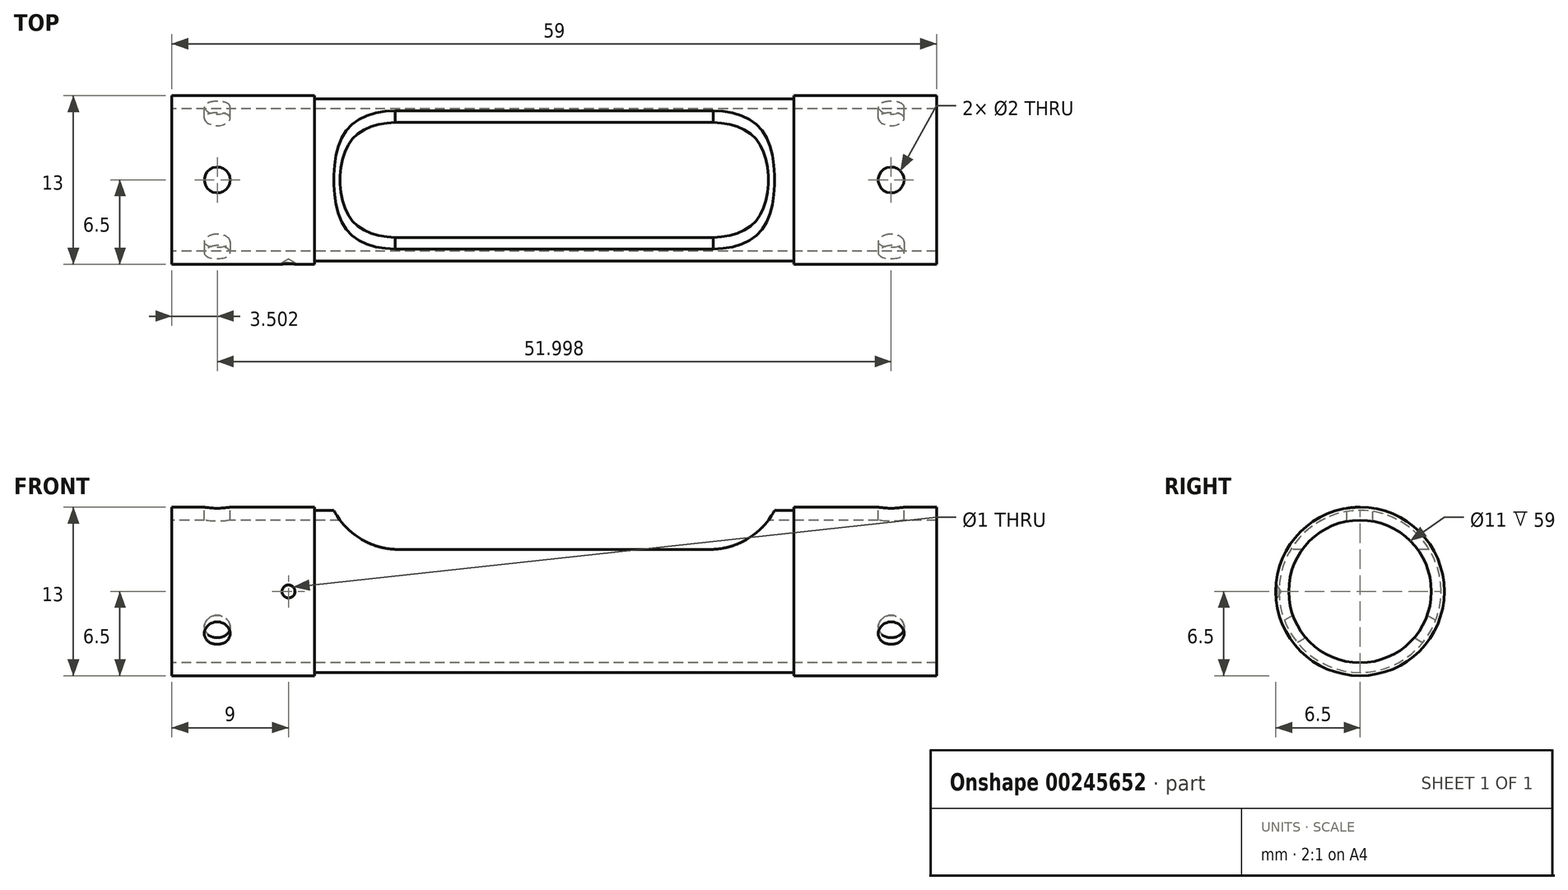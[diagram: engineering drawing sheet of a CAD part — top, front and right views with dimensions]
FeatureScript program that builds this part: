
annotation { "Feature Type Name" : "Feature", "Feature Type Description" : "" }
export const myFeature = defineFeature(function(context is Context, id is Id, definition is map)
    precondition{}
    {
        {
            var Q0;
            Q0=qCreatedBy(makeId("Right.planeOp"),FACE);
            var sketch = newSketch(context, id + "F0", { "sketchPlane" : qUnion([Q0])});
            skCircle(sketch, "E0", {"center": v(0, 0) * mm, "radius": 6.5 * mm});
            skCircle(sketch, "E1", {"center": v(0, 0) * mm, "radius": 5.5 * mm});
            skSolve(sketch);
        }
        {
            var Q0;
            Q0=makeQuery(id+"F0.imprint","IMPRINT",FACE,{"disambiguationData":[TD([[makeQuery(id+"F0.imprint","IMPRINT",EDGE,{"derivedFrom":sQuery(id+"F0.wireOp",EDGE,"E0")}),1.0]])]});
            extrude(context, id + "F1", {"entities" : qUnion([Q0]), "depth" : 11 * mm, "offsetDistance" : 25 * mm});
        }
        {
            var Q0;
            Q0=makeQuery(id+"F1.opExtrude","CAP_FACE",FACE,{"disambiguationData":[OSD([sQuery(id+"F0.wireOp",EDGE,"E0"),sQuery(id+"F0.wireOp",EDGE,"E1")])],"isStart":false});
            var sketch = newSketch(context, id + "F2", { "sketchPlane" : qUnion([Q0])});
            skCircle(sketch, "E2", {"center": v(0, 0) * mm, "radius": 6.25 * mm});
            skCircle(sketch, "E3", {"center": v(0, 0) * mm, "radius": 5.5 * mm});
            skSolve(sketch);
        }
        {
            var Q0;
            Q0=makeQuery(id+"F2.imprint","IMPRINT",FACE,{"disambiguationData":[TD([[makeQuery(id+"F2.imprint","IMPRINT",EDGE,{"derivedFrom":sQuery(id+"F2.wireOp",EDGE,"E2")}),1.0]])]});
            extrude(context, id + "F3", {"entities" : qUnion([Q0]), "operationType" : NewBodyOperationType.ADD, "depth" : 37 * mm, "offsetDistance" : 25 * mm});
        }
        {
            var Q0;
            Q0=makeQuery(id+"F3.opExtrude","CAP_FACE",FACE,{"disambiguationData":[OSD([sQuery(id+"F2.wireOp",EDGE,"E2"),sQuery(id+"F2.wireOp",EDGE,"E3")])],"isStart":false});
            var sketch = newSketch(context, id + "F4", { "sketchPlane" : qUnion([Q0])});
            skCircle(sketch, "E4", {"center": v(0, 0) * mm, "radius": 5.5 * mm});
            skCircle(sketch, "E5", {"center": v(0, 0) * mm, "radius": 6.5 * mm});
            skSolve(sketch);
        }
        {
            var Q0;
            Q0=makeQuery(id+"F4.imprint","IMPRINT",FACE,{"disambiguationData":[TD([[makeQuery(id+"F4.imprint","IMPRINT",EDGE,{"derivedFrom":sQuery(id+"F4.wireOp",EDGE,"E4")}),-1.0]])]});
            var Q1;
            Q1=makeQuery(id+"F4.imprint","IMPRINT",FACE,{"disambiguationData":[TD([[makeQuery(id+"F4.imprint","IMPRINT",EDGE,{"derivedFrom":sQuery(id+"F4.wireOp",EDGE,"E5")}),1.0]])]});
            extrude(context, id + "F5", {"entities" : qUnion([Q0, Q1]), "operationType" : NewBodyOperationType.ADD, "depth" : 11 * mm, "offsetDistance" : 25 * mm});
        }
        {
            var Q0;
            Q0=qCreatedBy(makeId("Front.planeOp"),FACE);
            cPlane(context, id + "F6", {"entities" : qUnion([Q0]), "cplaneType" : CPlaneType.OFFSET, "offset" : 6.5 * mm, "width" : 150 * mm, "height" : 150 * mm});
        }
        {
            var Q0;
            Q0=qCreatedBy(id+"F6.planeOp",FACE);
            var sketch = newSketch(context, id + "F7", { "sketchPlane" : qUnion([Q0])});
            skPoint(sketch, "E6", {"position": v(12.5, 6.25) * mm});
            skLineSegment(sketch, "E7", {"start": v(18.34, -6.25) * mm, "end": v(38.03, -6.25) * mm, "construction": true});
            skPoint(sketch, "E8.visualSharp", {"position": v(12.5, 3.25) * mm});
            skPoint(sketch, "E9", {"position": v(17.69, 3.25) * mm});
            skArc(sketch, "E10", {"start": v(12.5, 6.25) * mm, "mid": v(14.47, 4.11) * mm, "end": v(17.24, 3.25) * mm});
            skPoint(sketch, "E10.third.point", {"position": v(23.06, 9.25) * mm});
            skPoint(sketch, "E11.start.orphan", {"position": v(46.5, 9.25) * mm});
            skPoint(sketch, "E12.orphan", {"position": v(46.5, 3.25) * mm});
            skArc(sketch, "E13.MirrorCS", {"start": v(46.5, 6.25) * mm, "mid": v(44.53, 4.11) * mm, "end": v(41.76, 3.25) * mm});
            skLineSegment(sketch, "E14", {"start": v(17.24, 3.25) * mm, "end": v(41.76, 3.25) * mm});
            skLineSegment(sketch, "E15", {"start": v(12.5, 6.25) * mm, "end": v(46.5, 6.25) * mm});
            skSolve(sketch);
        }
        {
            var Q0;
            Q0 = qSketchRegion(id + "F7", true);
            extrude(context, id + "F8", {"entities" : qUnion([Q0]), "operationType" : NewBodyOperationType.REMOVE, "oppositeDirection" : true, "depth" : 25 * mm, "offsetDistance" : 25 * mm});
        }
        {
            var Q0;
            Q0=qCreatedBy(id+"F6.planeOp",FACE);
            var sketch = newSketch(context, id + "F9", { "sketchPlane" : qUnion([Q0])});
            skPoint(sketch, "E16", {"position": v(9, 0) * mm});
            skSolve(sketch);
        }
        {
            var Q0;
            Q0=sQuery(id+"F9.wireOp",VERTEX,"E16");
            var Q1;
            Q1=makeQuery(id+"F1.opExtrude","SWEPT_BODY",BODY,{"disambiguationData":[OSD([sQuery(id+"F0.wireOp",EDGE,"E0"),sQuery(id+"F0.wireOp",EDGE,"E1")])]});
            hole(context, id + "F10", {"style" : HoleStyle.SIMPLE, "endStyle" : HoleEndStyle.BLIND, "holeDiameter" : 1 * mm, "majorDiameter" : 5 * mm, "holeDepth" : .1 * mm, "isTappedThrough" : true, "tappedDepth" : 15 * mm, "tapClearance" : 0, "locations" : qUnion([Q0]), "scope" : qUnion([Q1]), "startStyle" : HoleStartStyle.SKETCH});
        }
        {
            var Q0;
            Q0=makeQuery(id+"F1.opExtrude","CAP_FACE",FACE,{"disambiguationData":[OSD([sQuery(id+"F0.wireOp",EDGE,"E0"),sQuery(id+"F0.wireOp",EDGE,"E1")])],"isStart":true});
            cPlane(context, id + "F11", {"entities" : qUnion([Q0]), "cplaneType" : CPlaneType.OFFSET, "offset" : 3.5 * mm, "oppositeDirection" : true, "width" : 150 * mm, "height" : 150 * mm});
        }
        {
            var Q0;
            Q0=qCreatedBy(id+"F11.planeOp",FACE);
            var sketch = newSketch(context, id + "F12", { "sketchPlane" : qUnion([Q0])});
            skLineSegment(sketch, "E17", {"start": v(0, 0) * mm, "end": v(0, 6.5) * mm});
            skLineSegment(sketch, "E18.1.0", {"start": v(0, 0) * mm, "end": v(-5.63, -3.25) * mm});
            skLineSegment(sketch, "E18.2.0", {"start": v(0, 0) * mm, "end": v(5.63, -3.25) * mm});
            skPoint(sketch, "E18.center", {"position": v(0, 0) * mm});
            skSolve(sketch);
        }
        {
            var Q0;
            Q0=sQuery(id+"F12.wireOp",VERTEX,"E17.end");
            var Q1;
            Q1=sQuery(id+"F12.wireOp",EDGE,"E17");
            cPlane(context, id + "F13", {"entities" : qUnion([Q0, Q1]), "cplaneType" : CPlaneType.CURVE_POINT, "offset" : 25 * mm, "width" : 150 * mm, "height" : 150 * mm});
        }
        {
            var Q0;
            Q0=qCreatedBy(id+"F13.planeOp",FACE);
            var sketch = newSketch(context, id + "F14", { "sketchPlane" : qUnion([Q0])});
            skPoint(sketch, "E19", {"position": v(3.5, 0) * mm});
            skPoint(sketch, "E20", {"position": v(0, 0) * mm});
            skCircle(sketch, "E21", {"center": v(3.5, 0) * mm, "radius": 1 * mm});
            skSolve(sketch);
        }
        {
            var Q0;
            Q0=makeQuery(id+"F14.imprint","IMPRINT",FACE,{"disambiguationData":[TD([[makeQuery(id+"F14.imprint","IMPRINT",EDGE,{"derivedFrom":sQuery(id+"F14.wireOp",EDGE,"E21")}),1.0]])]});
            extrude(context, id + "F15", {"entities" : qUnion([Q0]), "operationType" : NewBodyOperationType.REMOVE, "oppositeDirection" : true, "depth" : 5 * mm, "offsetDistance" : 25 * mm});
        }
        {
            var Q0;
            Q0=sQuery(id+"F12.wireOp",VERTEX,"E18.1.0.end");
            var Q1;
            Q1=sQuery(id+"F12.wireOp",EDGE,"E18.1.0");
            cPlane(context, id + "F16", {"entities" : qUnion([Q0, Q1]), "cplaneType" : CPlaneType.CURVE_POINT, "offset" : 25 * mm, "width" : 150 * mm, "height" : 150 * mm});
        }
        {
            var Q0;
            Q0=qCreatedBy(id+"F16.planeOp",FACE);
            var sketch = newSketch(context, id + "F17", { "sketchPlane" : qUnion([Q0])});
            skCircle(sketch, "E22", {"center": v(-3.5, 0) * mm, "radius": 1 * mm});
            skSolve(sketch);
        }
        {
            var Q0;
            Q0 = qSketchRegion(id + "F17", true);
            extrude(context, id + "F18", {"entities" : qUnion([Q0]), "operationType" : NewBodyOperationType.REMOVE, "oppositeDirection" : true, "depth" : 5 * mm, "offsetDistance" : 25 * mm});
        }
        {
            var Q0;
            Q0=sQuery(id+"F12.wireOp",VERTEX,"E18.2.0.end");
            var Q1;
            Q1=sQuery(id+"F12.wireOp",EDGE,"E18.2.0");
            cPlane(context, id + "F19", {"entities" : qUnion([Q0, Q1]), "cplaneType" : CPlaneType.CURVE_POINT, "offset" : 25 * mm, "width" : 150 * mm, "height" : 150 * mm});
        }
        {
            var Q0;
            Q0=qCreatedBy(id+"F19.planeOp",FACE);
            var sketch = newSketch(context, id + "F20", { "sketchPlane" : qUnion([Q0])});
            skCircle(sketch, "E23", {"center": v(3.5, 0) * mm, "radius": 1 * mm});
            skSolve(sketch);
        }
        {
            var Q0;
            Q0 = qSketchRegion(id + "F20", true);
            extrude(context, id + "F21", {"entities" : qUnion([Q0]), "operationType" : NewBodyOperationType.REMOVE, "oppositeDirection" : true, "depth" : 5 * mm, "offsetDistance" : 25 * mm});
        }
        {
            var Q0;
            Q0=makeQuery(id+"F5.opExtrude","CAP_FACE",FACE,{"disambiguationData":[OSD([sQuery(id+"F4.wireOp",EDGE,"E4"),sQuery(id+"F4.wireOp",EDGE,"E5")])],"isStart":false});
            cPlane(context, id + "F22", {"entities" : qUnion([Q0]), "cplaneType" : CPlaneType.OFFSET, "offset" : 3.5 * mm, "oppositeDirection" : true, "width" : 150 * mm, "height" : 150 * mm});
        }
        {
            var Q0;
            Q0=qCreatedBy(id+"F22.planeOp",FACE);
            var sketch = newSketch(context, id + "F23", { "sketchPlane" : qUnion([Q0])});
            skLineSegment(sketch, "E24", {"start": v(0, 0) * mm, "end": v(0, 6.5) * mm});
            skLineSegment(sketch, "E25.1.0", {"start": v(0, 0) * mm, "end": v(-5.63, -3.25) * mm});
            skLineSegment(sketch, "E25.2.0", {"start": v(0, 0) * mm, "end": v(5.63, -3.25) * mm});
            skPoint(sketch, "E25.center", {"position": v(0, 0) * mm});
            skSolve(sketch);
        }
        {
            var Q0;
            Q0=sQuery(id+"F23.wireOp",VERTEX,"E24.end");
            var Q1;
            Q1=sQuery(id+"F23.wireOp",EDGE,"E24");
            cPlane(context, id + "F24", {"entities" : qUnion([Q0, Q1]), "cplaneType" : CPlaneType.CURVE_POINT, "offset" : 25 * mm, "width" : 150 * mm, "height" : 150 * mm});
        }
        {
            var Q0;
            Q0=qCreatedBy(id+"F24.planeOp",FACE);
            var sketch = newSketch(context, id + "F25", { "sketchPlane" : qUnion([Q0])});
            skCircle(sketch, "E26", {"center": v(55.5, 0) * mm, "radius": 1 * mm});
            skSolve(sketch);
        }
        {
            var Q0;
            Q0 = qSketchRegion(id + "F25", true);
            extrude(context, id + "F26", {"entities" : qUnion([Q0]), "operationType" : NewBodyOperationType.REMOVE, "oppositeDirection" : true, "depth" : 5 * mm, "offsetDistance" : 25 * mm});
        }
        {
            var Q0;
            Q0=sQuery(id+"F23.wireOp",VERTEX,"E25.2.0.end");
            var Q1;
            Q1=sQuery(id+"F23.wireOp",EDGE,"E25.2.0");
            cPlane(context, id + "F27", {"entities" : qUnion([Q0, Q1]), "cplaneType" : CPlaneType.CURVE_POINT, "offset" : 25 * mm, "width" : 150 * mm, "height" : 150 * mm});
        }
        {
            var Q0;
            Q0=qCreatedBy(id+"F27.planeOp",FACE);
            var sketch = newSketch(context, id + "F28", { "sketchPlane" : qUnion([Q0])});
            skCircle(sketch, "E27", {"center": v(-55.5, 0) * mm, "radius": 1 * mm});
            skSolve(sketch);
        }
        {
            var Q0;
            Q0 = qSketchRegion(id + "F28", true);
            extrude(context, id + "F29", {"entities" : qUnion([Q0]), "operationType" : NewBodyOperationType.REMOVE, "oppositeDirection" : true, "depth" : 5 * mm, "offsetDistance" : 25 * mm});
        }
        {
            var Q0;
            Q0=sQuery(id+"F23.wireOp",VERTEX,"E25.1.0.end");
            var Q1;
            Q1=sQuery(id+"F23.wireOp",EDGE,"E25.1.0");
            cPlane(context, id + "F30", {"entities" : qUnion([Q0, Q1]), "cplaneType" : CPlaneType.CURVE_POINT, "offset" : 25 * mm, "width" : 150 * mm, "height" : 150 * mm});
        }
        {
            var Q0;
            Q0=qCreatedBy(id+"F30.planeOp",FACE);
            var sketch = newSketch(context, id + "F31", { "sketchPlane" : qUnion([Q0])});
            skCircle(sketch, "E28", {"center": v(55.5, 0) * mm, "radius": 1 * mm});
            skSolve(sketch);
        }
        {
            var Q0;
            Q0 = qSketchRegion(id + "F31", true);
            extrude(context, id + "F32", {"entities" : qUnion([Q0]), "operationType" : NewBodyOperationType.REMOVE, "oppositeDirection" : true, "depth" : 5 * mm, "offsetDistance" : 25 * mm});
        }
    });
